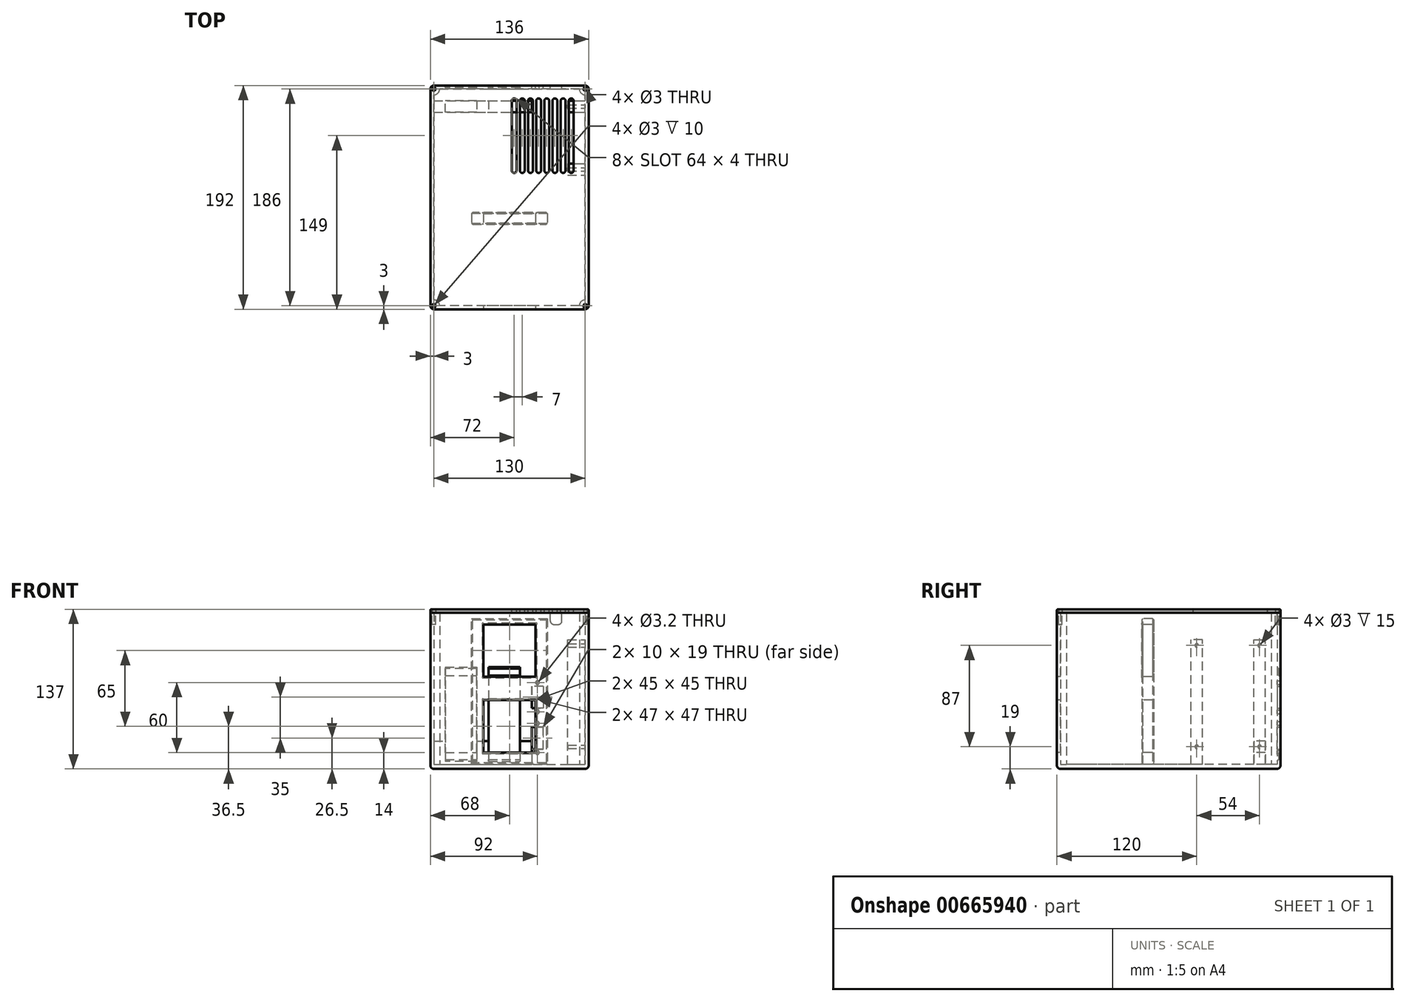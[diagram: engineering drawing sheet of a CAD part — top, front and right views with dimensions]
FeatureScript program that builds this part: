
annotation { "Feature Type Name" : "Feature", "Feature Type Description" : "" }
export const myFeature = defineFeature(function(context is Context, id is Id, definition is map)
    precondition{}
    {
        {
            var Q0;
            Q0=qCreatedBy(makeId("Top.planeOp"),FACE);
            var sketch = newSketch(context, id + "F0", { "sketchPlane" : qUnion([Q0])});
            skLineSegment(sketch, "E0.bottom", {"start": v(60, -93) * mm, "end": v(-60, -93) * mm});
            skLineSegment(sketch, "E0.top", {"start": v(60, 93) * mm, "end": v(-60, 93) * mm});
            skLineSegment(sketch, "E0.left", {"start": v(65, -88) * mm, "end": v(65, 88) * mm});
            skLineSegment(sketch, "E0.right", {"start": v(-65, -88) * mm, "end": v(-65, 88) * mm});
            skPoint(sketch, "E0.middle", {"position": v(0, 0) * mm});
            skLineSegment(sketch, "E1.bottom", {"start": v(68, -96) * mm, "end": v(-68, -96) * mm});
            skLineSegment(sketch, "E1.top", {"start": v(68, 96) * mm, "end": v(-68, 96) * mm});
            skLineSegment(sketch, "E1.left", {"start": v(68, -96) * mm, "end": v(68, 96) * mm});
            skLineSegment(sketch, "E1.right", {"start": v(-68, -96) * mm, "end": v(-68, 96) * mm});
            skArc(sketch, "E2", {"start": v(65, 88) * mm, "mid": v(61.46, 89.46) * mm, "end": v(60, 93) * mm});
            skArc(sketch, "E3.MirrorCS", {"start": v(65, -88) * mm, "mid": v(61.46, -89.46) * mm, "end": v(60, -93) * mm});
            skArc(sketch, "E4.MirrorCS", {"start": v(-65, -88) * mm, "mid": v(-61.46, -89.46) * mm, "end": v(-60, -93) * mm});
            skArc(sketch, "E5.MirrorCS", {"start": v(-65, 88) * mm, "mid": v(-61.46, 89.46) * mm, "end": v(-60, 93) * mm});
            skSolve(sketch);
        }
        {
            var Q0;
            Q0=makeQuery(id+"F0.imprint","IMPRINT",FACE,{"disambiguationData":[TD([[makeQuery(id+"F0.imprint","IMPRINT",EDGE,{"derivedFrom":sQuery(id+"F0.wireOp",EDGE,"E0.bottom")}),-1.0]])]});
            var Q1;
            Q1=makeQuery(id+"F0.imprint","IMPRINT",FACE,{"disambiguationData":[TD([[makeQuery(id+"F0.imprint","IMPRINT",EDGE,{"derivedFrom":sQuery(id+"F0.wireOp",EDGE,"E0.bottom")}),1.0]])]});
            extrude(context, id + "F1", {"entities" : qUnion([Q0, Q1]), "depth" : 4 * mm, "offsetDistance" : 25 * mm});
        }
        {
            var Q0;
            Q0=makeQuery(id+"F0.imprint","IMPRINT",FACE,{"disambiguationData":[TD([[makeQuery(id+"F0.imprint","IMPRINT",EDGE,{"derivedFrom":sQuery(id+"F0.wireOp",EDGE,"E0.bottom")}),1.0]])]});
            extrude(context, id + "F2", {"entities" : qUnion([Q0]), "operationType" : NewBodyOperationType.ADD, "depth" : 134 * mm, "offsetDistance" : 25 * mm});
        }
        {
            var Q0;
            {var subQ0=sQuery(id+"F0.wireOp",EDGE,"E1.bottom");Q0=makeQuery(id+"F2.boolean.opBoolean","MERGE",FACE,{"derivedFrom":[makeQuery(id+"F1.opExtrude","SWEPT_FACE",FACE,{"disambiguationData":[OSD([subQ0])]}),makeQuery(id+"F2.opExtrude","SWEPT_FACE",FACE,{"disambiguationData":[OSD([subQ0])]})]});}
            var sketch = newSketch(context, id + "F3", { "sketchPlane" : qUnion([Q0])});
            skLineSegment(sketch, "E6.bottom", {"start": v(22.5, 79) * mm, "end": v(-22.5, 79) * mm});
            skLineSegment(sketch, "E6.top", {"start": v(22.5, 124) * mm, "end": v(-22.5, 124) * mm});
            skLineSegment(sketch, "E6.left", {"start": v(22.5, 79) * mm, "end": v(22.5, 124) * mm});
            skLineSegment(sketch, "E6.right", {"start": v(-22.5, 79) * mm, "end": v(-22.5, 124) * mm});
            skPoint(sketch, "E6.middle", {"position": v(0, 101.5) * mm});
            skLineSegment(sketch, "E7.bottom", {"start": v(22.5, 14) * mm, "end": v(-22.5, 14) * mm});
            skLineSegment(sketch, "E7.top", {"start": v(22.5, 59) * mm, "end": v(-22.5, 59) * mm});
            skLineSegment(sketch, "E7.left", {"start": v(22.5, 14) * mm, "end": v(22.5, 59) * mm});
            skLineSegment(sketch, "E7.right", {"start": v(-22.5, 14) * mm, "end": v(-22.5, 59) * mm});
            skPoint(sketch, "E7.middle", {"position": v(0, 36.5) * mm});
            skSolve(sketch);
        }
        {
            var Q0;
            Q0=makeQuery(id+"F3.imprint","IMPRINT",FACE,{"disambiguationData":[TD([[makeQuery(id+"F3.imprint","IMPRINT",EDGE,{"derivedFrom":sQuery(id+"F3.wireOp",EDGE,"E6.bottom")}),-1.0]])]});
            var Q1;
            Q1=makeQuery(id+"F3.imprint","IMPRINT",FACE,{"disambiguationData":[TD([[makeQuery(id+"F3.imprint","IMPRINT",EDGE,{"derivedFrom":sQuery(id+"F3.wireOp",EDGE,"E7.bottom")}),-1.0]])]});
            extrude(context, id + "F4", {"entities" : qUnion([Q0, Q1]), "operationType" : NewBodyOperationType.REMOVE, "oppositeDirection" : true, "depth" : 25 * mm, "offsetDistance" : 25 * mm});
        }
        {
            var Q0;
            Q0=makeQuery(id+"F1.opExtrude","CAP_FACE",FACE,{"disambiguationData":[OSD([sQuery(id+"F0.wireOp",EDGE,"E1.bottom"),sQuery(id+"F0.wireOp",EDGE,"E1.top"),sQuery(id+"F0.wireOp",EDGE,"E1.left"),sQuery(id+"F0.wireOp",EDGE,"E1.right")])],"isStart":false});
            var sketch = newSketch(context, id + "F5", { "sketchPlane" : qUnion([Q0])});
            skLineSegment(sketch, "E8.bottom", {"start": v(-65, 73) * mm, "end": v(19, 73) * mm});
            skLineSegment(sketch, "E8.top", {"start": v(-65, 83) * mm, "end": v(19, 83) * mm});
            skLineSegment(sketch, "E8.left", {"start": v(-65, 73) * mm, "end": v(-65, 83) * mm});
            skLineSegment(sketch, "E8.right", {"start": v(19, 73) * mm, "end": v(19, 83) * mm});
            skSolve(sketch);
        }
        {
            var Q0;
            Q0=makeQuery(id+"F5.imprint","IMPRINT",FACE,{"disambiguationData":[TD([[makeQuery(id+"F5.imprint","IMPRINT",EDGE,{"derivedFrom":sQuery(id+"F5.wireOp",EDGE,"E8.bottom")}),1.0]])]});
            extrude(context, id + "F6", {"entities" : qUnion([Q0]), "operationType" : NewBodyOperationType.ADD, "depth" : 20 * mm, "offsetDistance" : 25 * mm});
        }
        {
            var Q0;
            Q0=makeQuery(id+"F6.opExtrude","SWEPT_FACE",FACE,{"disambiguationData":[OSD([sQuery(id+"F5.wireOp",EDGE,"E8.bottom")])]});
            var sketch = newSketch(context, id + "F7", { "sketchPlane" : qUnion([Q0])});
            skLineSegment(sketch, "E9", {"start": v(19, 24) * mm, "end": v(9, 24) * mm});
            skLineSegment(sketch, "E10", {"start": v(9, 24) * mm, "end": v(9, 14) * mm});
            skLineSegment(sketch, "E11", {"start": v(-18, 14) * mm, "end": v(9, 14) * mm});
            skLineSegment(sketch, "E12", {"start": v(-18, 14) * mm, "end": v(-18, 24) * mm});
            skLineSegment(sketch, "E13", {"start": v(-18, 24) * mm, "end": v(-28, 24) * mm});
            skLineSegment(sketch, "E14", {"start": v(-28, 24) * mm, "end": v(-28, 14) * mm});
            skLineSegment(sketch, "E15", {"start": v(-28, 14) * mm, "end": v(-55, 14) * mm});
            skLineSegment(sketch, "E16", {"start": v(-55, 14) * mm, "end": v(-55, 33.64) * mm});
            skLineSegment(sketch, "E17", {"start": v(-55, 33.64) * mm, "end": v(19, 33.64) * mm});
            skLineSegment(sketch, "E18", {"start": v(19, 33.64) * mm, "end": v(19, 24) * mm});
            skSolve(sketch);
        }
        {
            var Q0;
            Q0 = qSketchRegion(id + "F7", true);
            extrude(context, id + "F8", {"entities" : qUnion([Q0]), "operationType" : NewBodyOperationType.REMOVE, "oppositeDirection" : true, "depth" : 10 * mm, "offsetDistance" : 25 * mm});
        }
        {
            var Q0;
            Q0=makeQuery(id+"F2.opExtrude","SWEPT_FACE",FACE,{"disambiguationData":[OSD([sQuery(id+"F0.wireOp",EDGE,"E0.left")])]});
            var sketch = newSketch(context, id + "F9", { "sketchPlane" : qUnion([Q0])});
            skLineSegment(sketch, "E19.bottom", {"start": v(-73, 4) * mm, "end": v(-83, 4) * mm});
            skLineSegment(sketch, "E19.top", {"start": v(-73, 111) * mm, "end": v(-83, 111) * mm});
            skLineSegment(sketch, "E19.left", {"start": v(-73, 4) * mm, "end": v(-73, 111) * mm});
            skLineSegment(sketch, "E19.right", {"start": v(-83, 4) * mm, "end": v(-83, 111) * mm});
            skLineSegment(sketch, "E20.bottom", {"start": v(-29, 4) * mm, "end": v(-19, 4) * mm});
            skLineSegment(sketch, "E20.top", {"start": v(-29, 111) * mm, "end": v(-19, 111) * mm});
            skLineSegment(sketch, "E20.left", {"start": v(-29, 4) * mm, "end": v(-29, 111) * mm});
            skLineSegment(sketch, "E20.right", {"start": v(-19, 4) * mm, "end": v(-19, 111) * mm});
            skCircle(sketch, "E21", {"center": v(-78, 106) * mm, "radius": 1.5 * mm});
            skPoint(sketch, "E21.centerSnap0", {"position": v(-78, 111) * mm});
            skCircle(sketch, "E22", {"center": v(-24, 106) * mm, "radius": 1.5 * mm});
            skPoint(sketch, "E22.centerSnap0", {"position": v(-24, 111) * mm});
            skCircle(sketch, "E23", {"center": v(-24, 19) * mm, "radius": 1.5 * mm});
            skCircle(sketch, "E24", {"center": v(-78, 19) * mm, "radius": 1.5 * mm});
            skPoint(sketch, "E24.centerSnap0", {"position": v(-78, 4) * mm});
            skSolve(sketch);
        }
        {
            var Q0;
            Q0 = qSketchRegion(id + "F9", true);
            extrude(context, id + "F10", {"entities" : qUnion([Q0]), "operationType" : NewBodyOperationType.ADD, "depth" : 15 * mm, "offsetDistance" : 25 * mm});
        }
        {
            var Q0;
            Q0=makeQuery(id+"F2.opExtrude","CAP_FACE",FACE,{"disambiguationData":[OSD([sQuery(id+"F0.wireOp",EDGE,"E0.bottom"),sQuery(id+"F0.wireOp",EDGE,"E0.top"),sQuery(id+"F0.wireOp",EDGE,"E0.left"),sQuery(id+"F0.wireOp",EDGE,"E0.right"),sQuery(id+"F0.wireOp",EDGE,"E1.bottom"),sQuery(id+"F0.wireOp",EDGE,"E1.top"),sQuery(id+"F0.wireOp",EDGE,"E1.left"),sQuery(id+"F0.wireOp",EDGE,"E1.right"),sQuery(id+"F0.wireOp",EDGE,"E2"),sQuery(id+"F0.wireOp",EDGE,"E3.MirrorCS"),sQuery(id+"F0.wireOp",EDGE,"E4.MirrorCS"),sQuery(id+"F0.wireOp",EDGE,"E5.MirrorCS")])],"isStart":false});
            var sketch = newSketch(context, id + "F11", { "sketchPlane" : qUnion([Q0])});
            skCircle(sketch, "E25", {"center": v(65, 93) * mm, "radius": 1.5 * mm});
            skCircle(sketch, "E26", {"center": v(-65, 93) * mm, "radius": 1.5 * mm});
            skCircle(sketch, "E27", {"center": v(65, -93) * mm, "radius": 1.5 * mm});
            skCircle(sketch, "E28", {"center": v(-65, -93) * mm, "radius": 1.5 * mm});
            skSolve(sketch);
        }
        {
            var Q0;
            Q0 = qSketchRegion(id + "F11", true);
            extrude(context, id + "F12", {"entities" : qUnion([Q0]), "operationType" : NewBodyOperationType.REMOVE, "oppositeDirection" : true, "depth" : 10 * mm, "offsetDistance" : 25 * mm});
        }
        {
            var Q0;
            {var subQ0=sQuery(id+"F0.wireOp",EDGE,"E1.top");Q0=makeQuery(id+"F2.boolean.opBoolean","MERGE",FACE,{"derivedFrom":[makeQuery(id+"F1.opExtrude","SWEPT_FACE",FACE,{"disambiguationData":[OSD([subQ0])]}),makeQuery(id+"F2.opExtrude","SWEPT_FACE",FACE,{"disambiguationData":[OSD([subQ0])]})]});}
            var sketch = newSketch(context, id + "F13", { "sketchPlane" : qUnion([Q0])});
            skLineSegment(sketch, "E29.bottom", {"start": v(55, 14) * mm, "end": v(28, 14) * mm});
            skLineSegment(sketch, "E29.top", {"start": v(55, 80) * mm, "end": v(28, 80) * mm});
            skLineSegment(sketch, "E29.left", {"start": v(55, 14) * mm, "end": v(55, 80) * mm});
            skLineSegment(sketch, "E29.right", {"start": v(28, 14) * mm, "end": v(28, 80) * mm});
            skPoint(sketch, "E29.middle", {"position": v(41.5, 47) * mm});
            skLineSegment(sketch, "E30.bottom", {"start": v(18, 14) * mm, "end": v(-9, 14) * mm});
            skLineSegment(sketch, "E30.top", {"start": v(18, 80) * mm, "end": v(-9, 80) * mm});
            skLineSegment(sketch, "E30.left", {"start": v(18, 14) * mm, "end": v(18, 80) * mm});
            skLineSegment(sketch, "E30.right", {"start": v(-9, 14) * mm, "end": v(-9, 80) * mm});
            skPoint(sketch, "E30.middle", {"position": v(4.5, 47) * mm});
            skLineSegment(sketch, "E31.bottom", {"start": v(-45, 134) * mm, "end": v(-35, 134) * mm});
            skLineSegment(sketch, "E31.top", {"start": v(-45, 124) * mm, "end": v(-35, 124) * mm});
            skLineSegment(sketch, "E31.left", {"start": v(-45, 134) * mm, "end": v(-45, 124) * mm});
            skLineSegment(sketch, "E31.right", {"start": v(-35, 134) * mm, "end": v(-35, 124) * mm});
            skLineSegment(sketch, "E32.bottom", {"start": v(-29, 36) * mm, "end": v(-19, 36) * mm});
            skLineSegment(sketch, "E32.top", {"start": v(-29, 17) * mm, "end": v(-19, 17) * mm});
            skLineSegment(sketch, "E32.left", {"start": v(-29, 36) * mm, "end": v(-29, 17) * mm});
            skLineSegment(sketch, "E32.right", {"start": v(-19, 36) * mm, "end": v(-19, 17) * mm});
            skCircle(sketch, "E33", {"center": v(-24, 14) * mm, "radius": 1.6 * mm});
            skPoint(sketch, "E33.centerSnap0", {"position": v(-24, 17) * mm});
            skCircle(sketch, "E34", {"center": v(-24, 39) * mm, "radius": 1.6 * mm});
            skPoint(sketch, "E34.centerSnap0", {"position": v(-24, 36) * mm});
            skCircle(sketch, "E35", {"center": v(-24, 49) * mm, "radius": 1.6 * mm});
            skLineSegment(sketch, "E36.bottom", {"start": v(-19, 52) * mm, "end": v(-29, 52) * mm});
            skLineSegment(sketch, "E36.top", {"start": v(-19, 71) * mm, "end": v(-29, 71) * mm});
            skLineSegment(sketch, "E36.left", {"start": v(-19, 52) * mm, "end": v(-19, 71) * mm});
            skLineSegment(sketch, "E36.right", {"start": v(-29, 52) * mm, "end": v(-29, 71) * mm});
            skCircle(sketch, "E37", {"center": v(-24, 74) * mm, "radius": 1.6 * mm});
            skSolve(sketch);
        }
        {
            var Q0;
            Q0=makeQuery(id+"F13.imprint","IMPRINT",FACE,{"disambiguationData":[TD([[makeQuery(id+"F13.imprint","IMPRINT",EDGE,{"derivedFrom":sQuery(id+"F13.wireOp",EDGE,"E31.bottom")}),-1.0]])]});
            var Q1;
            Q1 = qSketchRegion(id + "F13", true);
            extrude(context, id + "F14", {"entities" : qUnion([Q0, Q1]), "operationType" : NewBodyOperationType.REMOVE, "oppositeDirection" : true, "depth" : 25 * mm, "offsetDistance" : 25 * mm});
        }
        {
            var Q0;
            Q0=makeQuery(id+"F2.opExtrude","SWEPT_FACE",FACE,{"disambiguationData":[OSD([sQuery(id+"F0.wireOp",EDGE,"E0.top")])]});
            var sketch = newSketch(context, id + "F15", { "sketchPlane" : qUnion([Q0])});
            skLineSegment(sketch, "E38.bottom", {"start": v(-55, 80) * mm, "end": v(-28, 80) * mm});
            skLineSegment(sketch, "E38.top", {"start": v(-55, 87.5) * mm, "end": v(-28, 87.5) * mm});
            skLineSegment(sketch, "E38.left", {"start": v(-55, 80) * mm, "end": v(-55, 87.5) * mm});
            skLineSegment(sketch, "E38.right", {"start": v(-28, 80) * mm, "end": v(-28, 87.5) * mm});
            skLineSegment(sketch, "E39.bottom", {"start": v(-18, 80) * mm, "end": v(9, 80) * mm});
            skLineSegment(sketch, "E39.top", {"start": v(-18, 87.5) * mm, "end": v(9, 87.5) * mm});
            skLineSegment(sketch, "E39.left", {"start": v(-18, 80) * mm, "end": v(-18, 87.5) * mm});
            skLineSegment(sketch, "E39.right", {"start": v(9, 80) * mm, "end": v(9, 87.5) * mm});
            skLineSegment(sketch, "E40.bottom", {"start": v(-28, 14) * mm, "end": v(-55, 14) * mm});
            skLineSegment(sketch, "E40.top", {"start": v(-28, 6.5) * mm, "end": v(-55, 6.5) * mm});
            skLineSegment(sketch, "E40.left", {"start": v(-28, 14) * mm, "end": v(-28, 6.5) * mm});
            skLineSegment(sketch, "E40.right", {"start": v(-55, 14) * mm, "end": v(-55, 6.5) * mm});
            skLineSegment(sketch, "E41.bottom", {"start": v(-18, 14) * mm, "end": v(9, 14) * mm});
            skLineSegment(sketch, "E41.top", {"start": v(-18, 6.5) * mm, "end": v(9, 6.5) * mm});
            skLineSegment(sketch, "E41.left", {"start": v(-18, 14) * mm, "end": v(-18, 6.5) * mm});
            skLineSegment(sketch, "E41.right", {"start": v(9, 14) * mm, "end": v(9, 6.5) * mm});
            skSolve(sketch);
        }
        {
            var Q0;
            Q0 = qSketchRegion(id + "F15", true);
            extrude(context, id + "F16", {"entities" : qUnion([Q0]), "operationType" : NewBodyOperationType.REMOVE, "oppositeDirection" : true, "depth" : 1.5 * mm, "offsetDistance" : 25 * mm});
        }
        {
            var Q0;
            Q0=makeQuery(id+"F16.boolean.opBoolean","COPY",EDGE,{"derivedFrom":makeQuery(id+"F16.opExtrude","CAP_EDGE",EDGE,{"disambiguationData":[OSD([sQuery(id+"F15.wireOp",EDGE,"E41.top")])],"isStart":false})});
            var Q1;
            Q1=makeQuery(id+"F16.boolean.opBoolean","COPY",EDGE,{"derivedFrom":makeQuery(id+"F16.opExtrude","CAP_EDGE",EDGE,{"disambiguationData":[OSD([sQuery(id+"F15.wireOp",EDGE,"E40.top")])],"isStart":false})});
            var Q2;
            Q2=makeQuery(id+"F16.boolean.opBoolean","COPY",EDGE,{"derivedFrom":makeQuery(id+"F16.opExtrude","CAP_EDGE",EDGE,{"disambiguationData":[OSD([sQuery(id+"F15.wireOp",EDGE,"E39.top")])],"isStart":false})});
            var Q3;
            Q3=makeQuery(id+"F16.boolean.opBoolean","COPY",EDGE,{"derivedFrom":makeQuery(id+"F16.opExtrude","CAP_EDGE",EDGE,{"disambiguationData":[OSD([sQuery(id+"F15.wireOp",EDGE,"E38.top")])],"isStart":false})});
            chamfer(context, id + "F17", {"entities" : qUnion([Q0, Q1, Q2, Q3]), "width" : 1.5 * mm, "tangentPropagation" : true});
        }
        {
            var Q0;
            {var subQ0=sQuery(id+"F0.wireOp",EDGE,"E1.right");var subQ1=sQuery(id+"F0.wireOp",EDGE,"E1.bottom");Q0=makeQuery(id+"F2.boolean.opBoolean","MERGE",EDGE,{"derivedFrom":[makeQuery(id+"F1.opExtrude","SWEPT_EDGE",EDGE,{"disambiguationData":[OSD([subQ1,subQ0])]}),makeQuery(id+"F2.opExtrude","SWEPT_EDGE",EDGE,{"disambiguationData":[OSD([subQ1,subQ0])]})]});}
            var Q1;
            {var subQ0=sQuery(id+"F0.wireOp",EDGE,"E1.left");var subQ1=sQuery(id+"F0.wireOp",EDGE,"E1.bottom");Q1=makeQuery(id+"F2.boolean.opBoolean","MERGE",EDGE,{"derivedFrom":[makeQuery(id+"F1.opExtrude","SWEPT_EDGE",EDGE,{"disambiguationData":[OSD([subQ1,subQ0])]}),makeQuery(id+"F2.opExtrude","SWEPT_EDGE",EDGE,{"disambiguationData":[OSD([subQ1,subQ0])]})]});}
            var Q2;
            {var subQ0=sQuery(id+"F0.wireOp",EDGE,"E1.left");var subQ1=sQuery(id+"F0.wireOp",EDGE,"E1.top");Q2=makeQuery(id+"F2.boolean.opBoolean","MERGE",EDGE,{"derivedFrom":[makeQuery(id+"F1.opExtrude","SWEPT_EDGE",EDGE,{"disambiguationData":[OSD([subQ1,subQ0])]}),makeQuery(id+"F2.opExtrude","SWEPT_EDGE",EDGE,{"disambiguationData":[OSD([subQ1,subQ0])]})]});}
            var Q3;
            {var subQ0=sQuery(id+"F0.wireOp",EDGE,"E1.right");var subQ1=sQuery(id+"F0.wireOp",EDGE,"E1.top");Q3=makeQuery(id+"F2.boolean.opBoolean","MERGE",EDGE,{"derivedFrom":[makeQuery(id+"F1.opExtrude","SWEPT_EDGE",EDGE,{"disambiguationData":[OSD([subQ1,subQ0])]}),makeQuery(id+"F2.opExtrude","SWEPT_EDGE",EDGE,{"disambiguationData":[OSD([subQ1,subQ0])]})]});}
            fillet(context, id + "F18", {"entities" : qUnion([Q0, Q1, Q2, Q3]), "radius" : 3 * mm, "tangentPropagation" : true, "allowEdgeOverflow" : false});
        }
        {
            var Q0;
            Q0=makeQuery(id+"F1.opExtrude","CAP_EDGE",EDGE,{"disambiguationData":[OSD([sQuery(id+"F0.wireOp",EDGE,"E1.bottom")])],"isStart":true});
            fillet(context, id + "F19", {"entities" : qUnion([Q0]), "radius" : 3 * mm, "tangentPropagation" : true, "allowEdgeOverflow" : false});
        }
        {
            var Q0;
            Q0=makeQuery(id+"F14.boolean.opBoolean","COPY",EDGE,{"derivedFrom":makeQuery(id+"F14.opExtrude","SWEPT_EDGE",EDGE,{"disambiguationData":[OSD([sQuery(id+"F13.wireOp",EDGE,"E31.top"),sQuery(id+"F13.wireOp",EDGE,"E31.left")])]})});
            var Q1;
            Q1=makeQuery(id+"F14.boolean.opBoolean","COPY",EDGE,{"derivedFrom":makeQuery(id+"F14.opExtrude","SWEPT_EDGE",EDGE,{"disambiguationData":[OSD([sQuery(id+"F13.wireOp",EDGE,"E31.top"),sQuery(id+"F13.wireOp",EDGE,"E31.right")])]})});
            fillet(context, id + "F20", {"entities" : qUnion([Q0, Q1]), "radius" : 3 * mm, "tangentPropagation" : true, "allowEdgeOverflow" : false});
        }
        {
            var Q0;
            Q0=makeQuery(id+"F2.opExtrude","SWEPT_FACE",FACE,{"disambiguationData":[OSD([sQuery(id+"F0.wireOp",EDGE,"E0.bottom")])]});
            cPlane(context, id + "F21", {"entities" : qUnion([Q0]), "cplaneType" : CPlaneType.OFFSET, "offset" : 70 * mm, "width" : 150 * mm, "height" : 150 * mm});
        }
        {
            var Q0;
            Q0=qCreatedBy(id+"F21.planeOp",FACE);
            var sketch = newSketch(context, id + "F22", { "sketchPlane" : qUnion([Q0])});
            skLineSegment(sketch, "E42.0", {"start": v(-22.5, 124) * mm, "end": v(22.5, 124) * mm});
            skLineSegment(sketch, "E43.0", {"start": v(-22.5, 79) * mm, "end": v(-22.5, 124) * mm});
            skLineSegment(sketch, "E44.0", {"start": v(22.5, 79) * mm, "end": v(22.5, 124) * mm});
            skLineSegment(sketch, "E45.0", {"start": v(-22.5, 79) * mm, "end": v(22.5, 79) * mm});
            skLineSegment(sketch, "E46.0", {"start": v(-22.5, 59) * mm, "end": v(22.5, 59) * mm});
            skLineSegment(sketch, "E47.0", {"start": v(22.5, 14) * mm, "end": v(22.5, 59) * mm});
            skLineSegment(sketch, "E48.0", {"start": v(-22.5, 14) * mm, "end": v(22.5, 14) * mm});
            skLineSegment(sketch, "E49.0", {"start": v(-22.5, 14) * mm, "end": v(-22.5, 59) * mm});
            skLineSegment(sketch, "E50.top", {"start": v(32.5, 129) * mm, "end": v(-32.5, 129) * mm});
            skLineSegment(sketch, "E50.left", {"start": v(32.5, 4) * mm, "end": v(32.5, 129) * mm});
            skLineSegment(sketch, "E50.right", {"start": v(-32.5, 4) * mm, "end": v(-32.5, 129) * mm});
            skLineSegment(sketch, "E51", {"start": v(-32.5, 4) * mm, "end": v(32.5, 4) * mm});
            skSolve(sketch);
        }
        {
            var Q0;
            Q0=makeQuery(id+"F22.imprint","IMPRINT",FACE,{"disambiguationData":[TD([[makeQuery(id+"F22.imprint","IMPRINT",EDGE,{"derivedFrom":sQuery(id+"F22.wireOp",EDGE,"E42.0")}),1.0]])]});
            extrude(context, id + "F23", {"entities" : qUnion([Q0]), "depth" : 10 * mm, "offsetDistance" : 25 * mm});
        }
        {
            var Q0;
            Q0=makeQuery(id+"F23.opExtrude","CAP_FACE",FACE,{"disambiguationData":[OSD([sQuery(id+"F22.wireOp",EDGE,"E42.0"),sQuery(id+"F22.wireOp",EDGE,"E43.0"),sQuery(id+"F22.wireOp",EDGE,"E44.0"),sQuery(id+"F22.wireOp",EDGE,"E45.0"),sQuery(id+"F22.wireOp",EDGE,"E46.0"),sQuery(id+"F22.wireOp",EDGE,"E47.0"),sQuery(id+"F22.wireOp",EDGE,"E48.0"),sQuery(id+"F22.wireOp",EDGE,"E49.0"),sQuery(id+"F22.wireOp",EDGE,"E50.top"),sQuery(id+"F22.wireOp",EDGE,"E50.left"),sQuery(id+"F22.wireOp",EDGE,"E50.right"),sQuery(id+"F22.wireOp",EDGE,"E51")])],"isStart":true});
            var Q1;
            Q1=makeQuery(id+"F23.opExtrude","CAP_FACE",FACE,{"disambiguationData":[OSD([sQuery(id+"F22.wireOp",EDGE,"E42.0"),sQuery(id+"F22.wireOp",EDGE,"E43.0"),sQuery(id+"F22.wireOp",EDGE,"E44.0"),sQuery(id+"F22.wireOp",EDGE,"E45.0"),sQuery(id+"F22.wireOp",EDGE,"E46.0"),sQuery(id+"F22.wireOp",EDGE,"E47.0"),sQuery(id+"F22.wireOp",EDGE,"E48.0"),sQuery(id+"F22.wireOp",EDGE,"E49.0"),sQuery(id+"F22.wireOp",EDGE,"E50.top"),sQuery(id+"F22.wireOp",EDGE,"E50.left"),sQuery(id+"F22.wireOp",EDGE,"E50.right"),sQuery(id+"F22.wireOp",EDGE,"E51")])],"isStart":false});
            chamfer(context, id + "F24", {"entities" : qUnion([Q0, Q1]), "width" : 1 * mm, "tangentPropagation" : true});
        }
        {
            var Q0;
            Q0=makeQuery(id+"F2.opExtrude","CAP_FACE",FACE,{"disambiguationData":[OSD([sQuery(id+"F0.wireOp",EDGE,"E0.bottom"),sQuery(id+"F0.wireOp",EDGE,"E0.top"),sQuery(id+"F0.wireOp",EDGE,"E0.left"),sQuery(id+"F0.wireOp",EDGE,"E0.right"),sQuery(id+"F0.wireOp",EDGE,"E1.bottom"),sQuery(id+"F0.wireOp",EDGE,"E1.top"),sQuery(id+"F0.wireOp",EDGE,"E1.left"),sQuery(id+"F0.wireOp",EDGE,"E1.right"),sQuery(id+"F0.wireOp",EDGE,"E2"),sQuery(id+"F0.wireOp",EDGE,"E3.MirrorCS"),sQuery(id+"F0.wireOp",EDGE,"E4.MirrorCS"),sQuery(id+"F0.wireOp",EDGE,"E5.MirrorCS")])],"isStart":false});
            cPlane(context, id + "F25", {"entities" : qUnion([Q0]), "cplaneType" : CPlaneType.OFFSET, "offset" : 0 * mm, "width" : 150 * mm, "height" : 150 * mm});
        }
        {
            var Q0;
            Q0=qCreatedBy(id+"F25.planeOp",FACE);
            var sketch = newSketch(context, id + "F26", { "sketchPlane" : qUnion([Q0])});
            skLineSegment(sketch, "E52.0.0", {"start": v(68, -93) * mm, "end": v(68, 93) * mm});
            skArc(sketch, "E52.0.1", {"start": v(68, 93) * mm, "mid": v(67.12, 95.12) * mm, "end": v(65, 96) * mm});
            skArc(sketch, "E52.0.5", {"start": v(60, 93) * mm, "mid": v(61.46, 89.46) * mm, "end": v(65, 88) * mm});
            skLineSegment(sketch, "E52.0.6", {"start": v(65, 88) * mm, "end": v(65, -88) * mm});
            skArc(sketch, "E52.0.7", {"start": v(65, -88) * mm, "mid": v(61.46, -89.46) * mm, "end": v(60, -93) * mm});
            skLineSegment(sketch, "E52.0.8", {"start": v(60, -93) * mm, "end": v(-60, -93) * mm});
            skArc(sketch, "E52.0.9", {"start": v(-60, -93) * mm, "mid": v(-61.46, -89.46) * mm, "end": v(-65, -88) * mm});
            skLineSegment(sketch, "E52.0.10", {"start": v(-65, -88) * mm, "end": v(-65, 88) * mm});
            skArc(sketch, "E52.0.11", {"start": v(-65, 88) * mm, "mid": v(-61.46, 89.46) * mm, "end": v(-60, 93) * mm});
            skLineSegment(sketch, "E52.0.12", {"start": v(-60, 93) * mm, "end": v(60, 93) * mm});
            skLineSegment(sketch, "E52.0.14", {"start": v(65, 96) * mm, "end": v(-65, 96) * mm});
            skArc(sketch, "E52.0.15", {"start": v(-65, 96) * mm, "mid": v(-67.12, 95.12) * mm, "end": v(-68, 93) * mm});
            skLineSegment(sketch, "E52.0.16", {"start": v(-68, 93) * mm, "end": v(-68, -93) * mm});
            skArc(sketch, "E52.0.17", {"start": v(-68, -93) * mm, "mid": v(-67.12, -95.12) * mm, "end": v(-65, -96) * mm});
            skLineSegment(sketch, "E52.0.18", {"start": v(-65, -96) * mm, "end": v(65, -96) * mm});
            skArc(sketch, "E52.0.19", {"start": v(65, -96) * mm, "mid": v(67.12, -95.12) * mm, "end": v(68, -93) * mm});
            skPoint(sketch, "E52.0.4.start.orphan", {"position": v(45, 93) * mm});
            skPoint(sketch, "E52.0.2.end.orphan", {"position": v(45, 96) * mm});
            skPoint(sketch, "E53.orphan", {"position": v(35, 93) * mm});
            skPoint(sketch, "E54.orphan", {"position": v(35, 96) * mm});
            skCircle(sketch, "E55.0", {"center": v(65, 93) * mm, "radius": 1.5 * mm});
            skCircle(sketch, "E56.0", {"center": v(-65, 93) * mm, "radius": 1.5 * mm});
            skCircle(sketch, "E57.0", {"center": v(65, -93) * mm, "radius": 1.5 * mm});
            skCircle(sketch, "E58.0", {"center": v(-65, -93) * mm, "radius": 1.5 * mm});
            skLineSegment(sketch, "E59.0", {"start": v(64, -87.08) * mm, "end": v(64, 87.08) * mm});
            skArc(sketch, "E59.1", {"start": v(59.08, -92) * mm, "mid": v(60.76, -88.76) * mm, "end": v(64, -87.08) * mm});
            skArc(sketch, "E59.2", {"start": v(64, 87.08) * mm, "mid": v(60.76, 88.76) * mm, "end": v(59.08, 92) * mm});
            skLineSegment(sketch, "E59.3", {"start": v(-59.08, -92) * mm, "end": v(59.08, -92) * mm});
            skLineSegment(sketch, "E59.4", {"start": v(59.08, 92) * mm, "end": v(-59.08, 92) * mm});
            skArc(sketch, "E59.5", {"start": v(-59.08, 92) * mm, "mid": v(-60.76, 88.76) * mm, "end": v(-64, 87.08) * mm});
            skLineSegment(sketch, "E59.6", {"start": v(-64, 87.08) * mm, "end": v(-64, -87.08) * mm});
            skArc(sketch, "E59.7", {"start": v(-64, -87.08) * mm, "mid": v(-60.76, -88.76) * mm, "end": v(-59.08, -92) * mm});
            skSolve(sketch);
        }
        {
            var Q0;
            Q0=makeQuery(id+"F26.imprint","IMPRINT",FACE,{"disambiguationData":[TD([[makeQuery(id+"F26.imprint","IMPRINT",EDGE,{"derivedFrom":sQuery(id+"F26.wireOp",EDGE,"E52.0.0")}),1.0]])]});
            var Q1;
            Q1=makeQuery(id+"F26.imprint","IMPRINT",FACE,{"disambiguationData":[TD([[makeQuery(id+"F26.imprint","IMPRINT",EDGE,{"derivedFrom":sQuery(id+"F26.wireOp",EDGE,"E52.0.5")}),-1.0]])]});
            var Q2;
            Q2=makeQuery(id+"F26.imprint","IMPRINT",FACE,{"disambiguationData":[TD([[makeQuery(id+"F26.imprint","IMPRINT",EDGE,{"derivedFrom":sQuery(id+"F26.wireOp",EDGE,"E59.0")}),1.0]])]});
            extrude(context, id + "F27", {"entities" : qUnion([Q0, Q1, Q2]), "depth" : 3 * mm, "offsetDistance" : 25 * mm});
        }
        {
            var Q0;
            Q0=makeQuery(id+"F27.opExtrude","CAP_FACE",FACE,{"disambiguationData":[OSD([sQuery(id+"F26.wireOp",EDGE,"E52.0.0"),sQuery(id+"F26.wireOp",EDGE,"E52.0.1"),sQuery(id+"F26.wireOp",EDGE,"E52.0.14"),sQuery(id+"F26.wireOp",EDGE,"E52.0.15"),sQuery(id+"F26.wireOp",EDGE,"E52.0.16"),sQuery(id+"F26.wireOp",EDGE,"E52.0.17"),sQuery(id+"F26.wireOp",EDGE,"E52.0.18"),sQuery(id+"F26.wireOp",EDGE,"E52.0.19"),sQuery(id+"F26.wireOp",EDGE,"E55.0"),sQuery(id+"F26.wireOp",EDGE,"E56.0"),sQuery(id+"F26.wireOp",EDGE,"E57.0"),sQuery(id+"F26.wireOp",EDGE,"E58.0")])],"isStart":false});
            fillet(context, id + "F28", {"entities" : qUnion([Q0]), "radius" : 1 * mm, "tangentPropagation" : true, "allowEdgeOverflow" : false});
        }
        {
            var Q0;
            Q0=makeQuery(id+"F27.opExtrude","CAP_FACE",FACE,{"disambiguationData":[OSD([sQuery(id+"F26.wireOp",EDGE,"E52.0.0"),sQuery(id+"F26.wireOp",EDGE,"E52.0.1"),sQuery(id+"F26.wireOp",EDGE,"E52.0.14"),sQuery(id+"F26.wireOp",EDGE,"E52.0.15"),sQuery(id+"F26.wireOp",EDGE,"E52.0.16"),sQuery(id+"F26.wireOp",EDGE,"E52.0.17"),sQuery(id+"F26.wireOp",EDGE,"E52.0.18"),sQuery(id+"F26.wireOp",EDGE,"E52.0.19"),sQuery(id+"F26.wireOp",EDGE,"E55.0"),sQuery(id+"F26.wireOp",EDGE,"E56.0"),sQuery(id+"F26.wireOp",EDGE,"E57.0"),sQuery(id+"F26.wireOp",EDGE,"E58.0")])],"isStart":false});
            var sketch = newSketch(context, id + "F29", { "sketchPlane" : qUnion([Q0])});
            skLineSegment(sketch, "E60.left", {"start": v(2, 83) * mm, "end": v(2, 23) * mm});
            skLineSegment(sketch, "E60.right", {"start": v(6, 83) * mm, "end": v(6, 23) * mm});
            skArc(sketch, "E61", {"start": v(2, 83) * mm, "mid": v(4, 85) * mm, "end": v(6, 83) * mm});
            skArc(sketch, "E62", {"start": v(2, 23) * mm, "mid": v(4, 21) * mm, "end": v(6, 23) * mm});
            skLineSegment(sketch, "E63.1.0.0", {"start": v(13, 83) * mm, "end": v(13, 23) * mm});
            skLineSegment(sketch, "E63.1.0.1", {"start": v(9, 83) * mm, "end": v(9, 23) * mm});
            skArc(sketch, "E63.1.0.2", {"start": v(9, 83) * mm, "mid": v(11, 85) * mm, "end": v(13, 83) * mm});
            skArc(sketch, "E63.1.0.3", {"start": v(9, 23) * mm, "mid": v(11, 21) * mm, "end": v(13, 23) * mm});
            skLineSegment(sketch, "E63.2.0.0", {"start": v(20, 83) * mm, "end": v(20, 23) * mm});
            skLineSegment(sketch, "E63.2.0.1", {"start": v(16, 83) * mm, "end": v(16, 23) * mm});
            skArc(sketch, "E63.2.0.2", {"start": v(16, 83) * mm, "mid": v(18, 85) * mm, "end": v(20, 83) * mm});
            skArc(sketch, "E63.2.0.3", {"start": v(16, 23) * mm, "mid": v(18, 21) * mm, "end": v(20, 23) * mm});
            skLineSegment(sketch, "E63.3.0.0", {"start": v(27, 83) * mm, "end": v(27, 23) * mm});
            skLineSegment(sketch, "E63.3.0.1", {"start": v(23, 83) * mm, "end": v(23, 23) * mm});
            skArc(sketch, "E63.3.0.2", {"start": v(23, 83) * mm, "mid": v(25, 85) * mm, "end": v(27, 83) * mm});
            skArc(sketch, "E63.3.0.3", {"start": v(23, 23) * mm, "mid": v(25, 21) * mm, "end": v(27, 23) * mm});
            skLineSegment(sketch, "E63.4.0.0", {"start": v(34, 83) * mm, "end": v(34, 23) * mm});
            skLineSegment(sketch, "E63.4.0.1", {"start": v(30, 83) * mm, "end": v(30, 23) * mm});
            skArc(sketch, "E63.4.0.2", {"start": v(30, 83) * mm, "mid": v(32, 85) * mm, "end": v(34, 83) * mm});
            skArc(sketch, "E63.4.0.3", {"start": v(30, 23) * mm, "mid": v(32, 21) * mm, "end": v(34, 23) * mm});
            skLineSegment(sketch, "E63.5.0.0", {"start": v(41, 83) * mm, "end": v(41, 23) * mm});
            skLineSegment(sketch, "E63.5.0.1", {"start": v(37, 83) * mm, "end": v(37, 23) * mm});
            skArc(sketch, "E63.5.0.2", {"start": v(37, 83) * mm, "mid": v(39, 85) * mm, "end": v(41, 83) * mm});
            skArc(sketch, "E63.5.0.3", {"start": v(37, 23) * mm, "mid": v(39, 21) * mm, "end": v(41, 23) * mm});
            skLineSegment(sketch, "E63.6.0.0", {"start": v(48, 83) * mm, "end": v(48, 23) * mm});
            skLineSegment(sketch, "E63.6.0.1", {"start": v(44, 83) * mm, "end": v(44, 23) * mm});
            skArc(sketch, "E63.6.0.2", {"start": v(44, 83) * mm, "mid": v(46, 85) * mm, "end": v(48, 83) * mm});
            skArc(sketch, "E63.6.0.3", {"start": v(44, 23) * mm, "mid": v(46, 21) * mm, "end": v(48, 23) * mm});
            skLineSegment(sketch, "E63.7.0.0", {"start": v(55, 83) * mm, "end": v(55, 23) * mm});
            skLineSegment(sketch, "E63.7.0.1", {"start": v(51, 83) * mm, "end": v(51, 23) * mm});
            skArc(sketch, "E63.7.0.2", {"start": v(51, 83) * mm, "mid": v(53, 85) * mm, "end": v(55, 83) * mm});
            skArc(sketch, "E63.7.0.3", {"start": v(51, 23) * mm, "mid": v(53, 21) * mm, "end": v(55, 23) * mm});
            skLineSegment(sketch, "E63.direction1", {"start": v(2, 23) * mm, "end": v(9, 23) * mm, "construction": true});
            skLineSegment(sketch, "E63.direction2", {"start": v(2, 23) * mm, "end": v(2, 23) * mm});
            skSolve(sketch);
        }
        {
            var Q0;
            Q0 = qSketchRegion(id + "F29", true);
            extrude(context, id + "F30", {"entities" : qUnion([Q0]), "operationType" : NewBodyOperationType.REMOVE, "oppositeDirection" : true, "depth" : 25 * mm, "offsetDistance" : 25 * mm});
        }
    });
